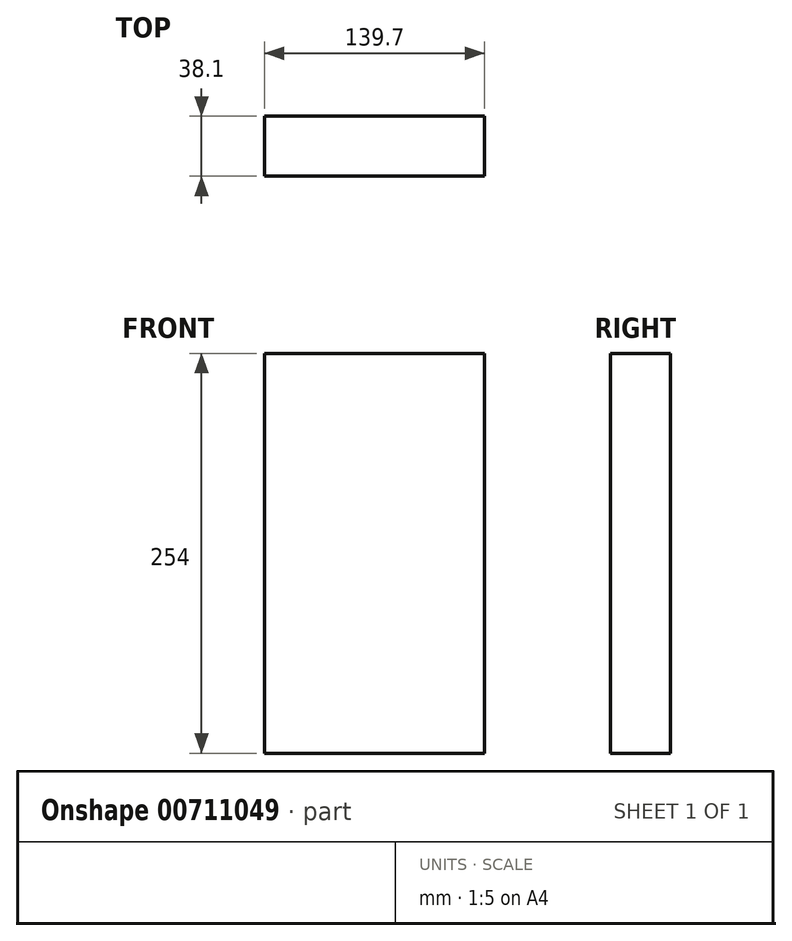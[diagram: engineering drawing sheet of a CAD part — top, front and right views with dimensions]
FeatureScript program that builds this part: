
annotation { "Feature Type Name" : "Feature", "Feature Type Description" : "" }
export const myFeature = defineFeature(function(context is Context, id is Id, definition is map)
    precondition{}
    {
        {
            var Q0;
            Q0=qCreatedBy(makeId("Top.planeOp"),FACE);
            var sketch = newSketch(context, id + "F0", { "sketchPlane" : qUnion([Q0])});
            skLineSegment(sketch, "E0.bottom", {"start": v(69.85, 19.05) * mm, "end": v(-69.85, 19.05) * mm});
            skLineSegment(sketch, "E0.top", {"start": v(69.85, -19.05) * mm, "end": v(-69.85, -19.05) * mm});
            skLineSegment(sketch, "E0.left", {"start": v(69.85, 19.05) * mm, "end": v(69.85, -19.05) * mm});
            skLineSegment(sketch, "E0.right", {"start": v(-69.85, 19.05) * mm, "end": v(-69.85, -19.05) * mm});
            skPoint(sketch, "E0.middle", {"position": v(0, 0) * mm});
            skSolve(sketch);
        }
        {
            var Q0;
            Q0=makeQuery(id+"F0.imprint","IMPRINT",FACE,{"disambiguationData":[TD([[makeQuery(id+"F0.imprint","IMPRINT",EDGE,{"derivedFrom":sQuery(id+"F0.wireOp",EDGE,"E0.bottom")}),1.0]])]});
            extrude(context, id + "F1", {"entities" : qUnion([Q0]), "depth" : 254 * mm, "offsetDistance" : 25.4 * mm});
        }
    });
